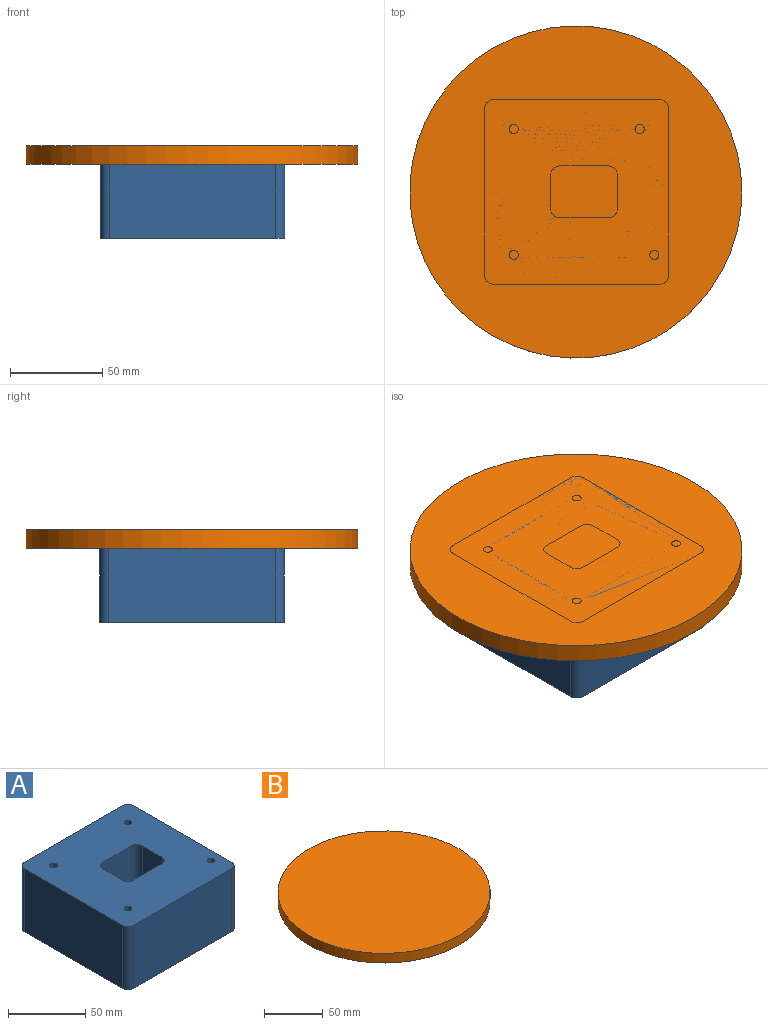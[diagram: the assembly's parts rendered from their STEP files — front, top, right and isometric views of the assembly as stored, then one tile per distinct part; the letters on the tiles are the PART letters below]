
ASSEMBLY  parts=2 mates=2
PART A: 30 faces, bbox 100x100x50 mm
  f0: plane 90x50mm, normal (1,0,0), area 4500mm2, adj f1,f15,f16,f17
  f1: cylinder r=5mm len=50mm, axis (0,0,-1), area 392.7mm2, adj f0,f2,f16,f17
  f2: plane 90x50mm, normal (0,1,0), area 4500mm2, adj f1,f3,f16,f17
  f3: cylinder r=5mm len=50mm, axis (0,0,-1), area 392.7mm2, adj f2,f4,f16,f17
  f4: plane 90x50mm, normal (-1,0,0), area 4500mm2, adj f3,f5,f16,f17
  f5: cylinder r=5mm len=50mm, axis (0,0,-1), area 392.7mm2, adj f4,f6,f16,f17
  f6: plane 90x50mm, normal (0,-1,0), area 4500mm2, adj f5,f15,f16,f17
  f7: cylinder r=5mm len=50mm, axis (0,0,-1), area 392.7mm2, adj f8,f14,f16,f17
  f8: plane 50x18.18mm, normal (1,0,0), area 909mm2, adj f7,f9,f16,f17
  f9: cylinder r=5mm len=50mm, axis (0,0,-1), area 392.7mm2, adj f8,f10,f16,f17
  f10: plane 50x26.18mm, normal (0,-1,0), area 1309mm2, adj f9,f11,f16,f17
  f11: cylinder r=5mm len=50mm, axis (0,0,-1), area 392.7mm2, adj f10,f12,f16,f17
  f12: plane 50x18.18mm, normal (-1,0,0), area 909mm2, adj f11,f13,f16,f17
  f13: cylinder r=5mm len=50mm, axis (0,0,-1), area 392.7mm2, adj f12,f14,f16,f17
  f14: plane 50x26.18mm, normal (0,1,0), area 1309mm2, adj f7,f13,f16,f17
  f15: cylinder r=5mm len=50mm, axis (0,0,-1), area 392.7mm2, adj f0,f6,f16,f17
  f16: plane 100x100mm, normal (0,0,1), area 8901.9mm2, adj f0,f1,f2,f3,f4,f5,f6,f7
  f17: plane 100x100mm, normal (0,0,-1), area 8766.6mm2, adj f0,f1,f2,f3,f4,f5,f6,f7
  f18: cylinder r=2.5mm len=46mm, axis (0,0,-1), area 722.6mm2, adj f16,f19
  f19: plane 8.25x8.25mm, normal (0,0,-1), area 33.8mm2, adj f18,f20
  f20: cylinder r=4.12mm len=8.25mm, axis (0,0,-1), area 103.7mm2, adj f17,f19
  f21: cylinder r=2.5mm len=46mm, axis (0,0,-1), area 722.6mm2, adj f16,f22
  f22: plane 8.25x8.25mm, normal (0,0,-1), area 33.8mm2, adj f21,f23
  f23: cylinder r=4.12mm len=8.25mm, axis (0,0,-1), area 103.7mm2, adj f17,f22
  f24: cylinder r=2.5mm len=46mm, axis (0,0,-1), area 722.6mm2, adj f16,f25
  f25: plane 8.25x8.25mm, normal (0,0,-1), area 33.8mm2, adj f24,f26
  f26: cylinder r=4.12mm len=8.25mm, axis (0,0,-1), area 103.7mm2, adj f17,f25
  f27: cylinder r=2.5mm len=46mm, axis (0,0,-1), area 722.6mm2, adj f16,f28
  f28: plane 8.25x8.25mm, normal (0,0,-1), area 33.8mm2, adj f27,f29
  f29: cylinder r=4.12mm len=8.25mm, axis (0,0,-1), area 103.7mm2, adj f17,f28
PART B: 3 faces, bbox 180x180x10 mm
  f0: cylinder r=90mm len=180mm, axis (0,0,-1), area 5654.9mm2, adj f1,f2
  f1: plane 180x180mm, normal (0,0,1), area 25446.9mm2, adj f0
  f2: plane 180x180mm, normal (0,0,-1), area 25446.9mm2, adj f0
PLACE A t=(-121.52,-44.17,-3.62)mm
PLACE B t=(-122.16,-32.9,36.38)mm
MATE revolute B.f0 <-> A.f16  axis (0,0,1) through (-122.16,-32.9,46.38)mm
MATE parallel B.f0 <-> B.f0  axis (0,0,-1) through (-122.16,-32.9,36.38)mm
